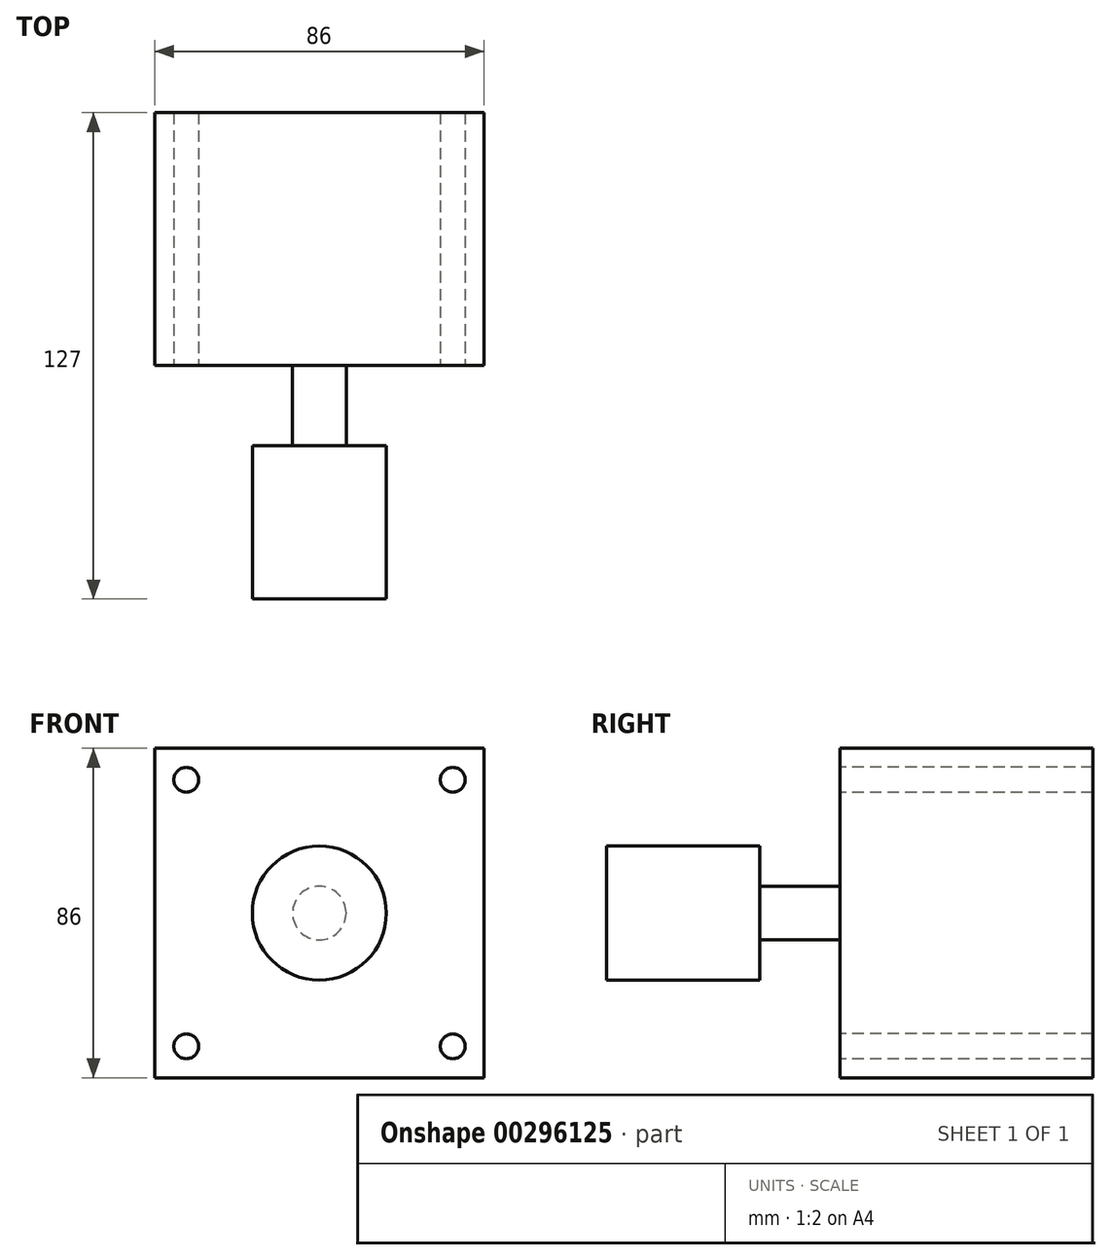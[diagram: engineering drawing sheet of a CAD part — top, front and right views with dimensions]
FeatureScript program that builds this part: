
annotation { "Feature Type Name" : "Feature", "Feature Type Description" : "" }
export const myFeature = defineFeature(function(context is Context, id is Id, definition is map)
    precondition{}
    {
        {
            var Q0;
            Q0=qCreatedBy(makeId("Front.planeOp"),FACE);
            var sketch = newSketch(context, id + "F0", { "sketchPlane" : qUnion([Q0])});
            skLineSegment(sketch, "E0.bottom", {"start": v(43, 43) * mm, "end": v(-43, 43) * mm});
            skLineSegment(sketch, "E0.top", {"start": v(43, -43) * mm, "end": v(-43, -43) * mm});
            skLineSegment(sketch, "E0.left", {"start": v(43, 43) * mm, "end": v(43, -43) * mm});
            skLineSegment(sketch, "E0.right", {"start": v(-43, 43) * mm, "end": v(-43, -43) * mm});
            skPoint(sketch, "E0.middle", {"position": v(0, 0) * mm});
            skCircle(sketch, "E1", {"center": v(-34.75, 34.8) * mm, "radius": 3.25 * mm});
            skCircle(sketch, "E2", {"center": v(34.85, 34.8) * mm, "radius": 3.25 * mm});
            skCircle(sketch, "E3", {"center": v(34.85, -34.8) * mm, "radius": 3.25 * mm});
            skCircle(sketch, "E4", {"center": v(-34.75, -34.8) * mm, "radius": 3.25 * mm});
            skSolve(sketch);
        }
        {
            var Q0;
            Q0=makeQuery(id+"F0.imprint","IMPRINT",FACE,{"disambiguationData":[TD([[makeQuery(id+"F0.imprint","IMPRINT",EDGE,{"derivedFrom":sQuery(id+"F0.wireOp",EDGE,"E0.bottom")}),1.0]])]});
            extrude(context, id + "F1", {"entities" : qUnion([Q0]), "oppositeDirection" : true, "depth" : 66 * mm, "offsetDistance" : 25 * mm});
        }
        {
            var Q0;
            Q0=makeQuery(id+"F1.opExtrude","CAP_FACE",FACE,{"disambiguationData":[OSD([sQuery(id+"F0.wireOp",EDGE,"E0.bottom"),sQuery(id+"F0.wireOp",EDGE,"E0.top"),sQuery(id+"F0.wireOp",EDGE,"E0.left"),sQuery(id+"F0.wireOp",EDGE,"E0.right")])],"isStart":true});
            var sketch = newSketch(context, id + "F2", { "sketchPlane" : qUnion([Q0])});
            skCircle(sketch, "E5", {"center": v(0, 0) * mm, "radius": 7 * mm});
            skSolve(sketch);
        }
        {
            var Q0;
            Q0 = qSketchRegion(id + "F2", true);
            extrude(context, id + "F3", {"entities" : qUnion([Q0]), "operationType" : NewBodyOperationType.ADD, "depth" : 36 * mm});
        }
        {
            var Q0;
            Q0=makeQuery(id+"F1.opExtrude","CAP_FACE",FACE,{"disambiguationData":[OSD([sQuery(id+"F0.wireOp",EDGE,"E0.bottom"),sQuery(id+"F0.wireOp",EDGE,"E0.top"),sQuery(id+"F0.wireOp",EDGE,"E0.left"),sQuery(id+"F0.wireOp",EDGE,"E0.right")])],"isStart":true});
            cPlane(context, id + "F4", {"entities" : qUnion([Q0]), "cplaneType" : CPlaneType.OFFSET, "offset" : 21 * mm, "width" : 150 * mm, "height" : 150 * mm});
        }
        {
            var Q0;
            Q0=qCreatedBy(id+"F4.planeOp",FACE);
            var sketch = newSketch(context, id + "F5", { "sketchPlane" : qUnion([Q0])});
            skCircle(sketch, "E6", {"center": v(0, 0) * mm, "radius": 17.5 * mm});
            skSolve(sketch);
        }
        {
            var Q0;
            Q0 = qSketchRegion(id + "F5", true);
            extrude(context, id + "F6", {"entities" : qUnion([Q0]), "operationType" : NewBodyOperationType.ADD, "depth" : 40 * mm, "offsetDistance" : 25 * mm});
        }
    });
